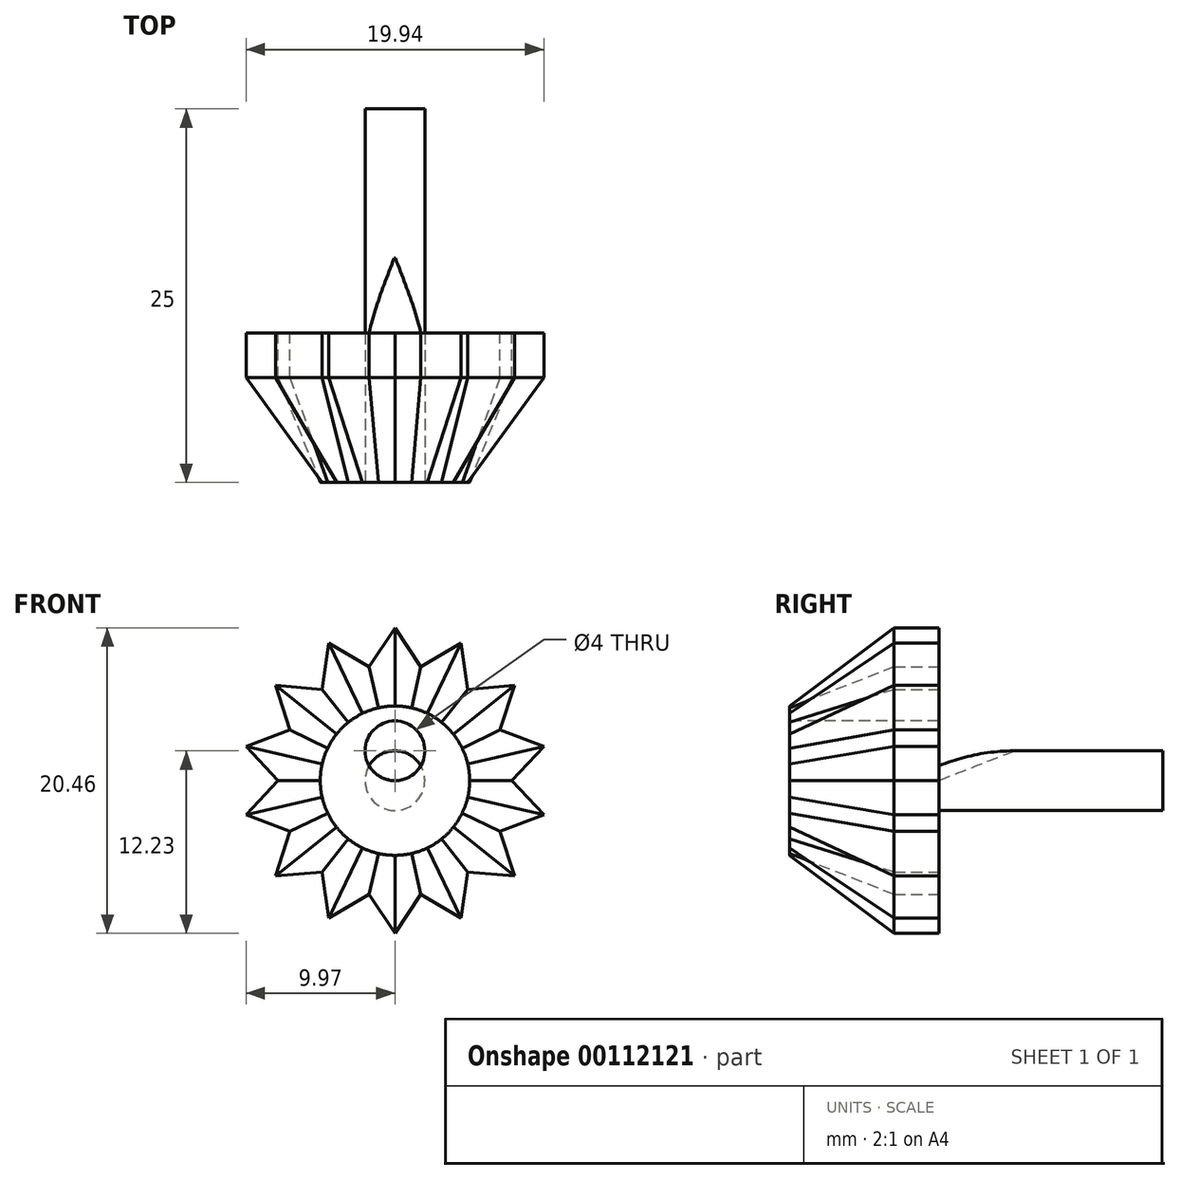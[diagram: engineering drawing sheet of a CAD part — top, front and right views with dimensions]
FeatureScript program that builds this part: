
annotation { "Feature Type Name" : "Feature", "Feature Type Description" : "" }
export const myFeature = defineFeature(function(context is Context, id is Id, definition is map)
    precondition{}
    {
        {
            var Q0;
            Q0=qCreatedBy(makeId("Front.planeOp"),FACE);
            var sketch = newSketch(context, id + "F0", { "sketchPlane" : qUnion([Q0])});
            skCircle(sketch, "E0", {"center": v(0, 0) * mm, "radius": 7.5 * mm, "construction": true});
            skLineSegment(sketch, "E1", {"start": v(-2, 7.23) * mm, "end": v(0, 10.23) * mm});
            skLineSegment(sketch, "E2", {"start": v(0, 10.23) * mm, "end": v(2, 7.23) * mm});
            skLineSegment(sketch, "E3", {"start": v(2, 7.23) * mm, "end": v(-2, 7.23) * mm, "construction": true});
            skLineSegment(sketch, "E4.1.0", {"start": v(-4.94, 5.64) * mm, "end": v(-4.44, 9.22) * mm});
            skLineSegment(sketch, "E4.1.1", {"start": v(-4.44, 9.22) * mm, "end": v(-1.33, 7.38) * mm});
            skLineSegment(sketch, "E4.2.0", {"start": v(-6.9, 2.94) * mm, "end": v(-8, 6.38) * mm});
            skLineSegment(sketch, "E4.2.1", {"start": v(-8, 6.38) * mm, "end": v(-4.4, 6.07) * mm});
            skLineSegment(sketch, "E4.3.0", {"start": v(-7.5, -0.34) * mm, "end": v(-9.97, 2.28) * mm});
            skLineSegment(sketch, "E4.3.1", {"start": v(-9.97, 2.28) * mm, "end": v(-6.6, 3.56) * mm});
            skLineSegment(sketch, "E4.4.0", {"start": v(-6.6, -3.56) * mm, "end": v(-9.97, -2.28) * mm});
            skLineSegment(sketch, "E4.4.1", {"start": v(-9.97, -2.28) * mm, "end": v(-7.5, 0.34) * mm});
            skLineSegment(sketch, "E4.5.0", {"start": v(-4.4, -6.07) * mm, "end": v(-8, -6.38) * mm});
            skLineSegment(sketch, "E4.5.1", {"start": v(-8, -6.38) * mm, "end": v(-6.9, -2.94) * mm});
            skLineSegment(sketch, "E4.6.0", {"start": v(-1.33, -7.38) * mm, "end": v(-4.44, -9.22) * mm});
            skLineSegment(sketch, "E4.6.1", {"start": v(-4.44, -9.22) * mm, "end": v(-4.94, -5.64) * mm});
            skLineSegment(sketch, "E4.7.0", {"start": v(2, -7.23) * mm, "end": v(0, -10.23) * mm});
            skLineSegment(sketch, "E4.7.1", {"start": v(0, -10.23) * mm, "end": v(-2, -7.23) * mm});
            skLineSegment(sketch, "E4.8.0", {"start": v(4.94, -5.64) * mm, "end": v(4.44, -9.22) * mm});
            skLineSegment(sketch, "E4.8.1", {"start": v(4.44, -9.22) * mm, "end": v(1.33, -7.38) * mm});
            skLineSegment(sketch, "E4.9.0", {"start": v(6.9, -2.94) * mm, "end": v(8, -6.38) * mm});
            skLineSegment(sketch, "E4.9.1", {"start": v(8, -6.38) * mm, "end": v(4.4, -6.07) * mm});
            skLineSegment(sketch, "E5.1.10.0", {"start": v(7.5, 0.34) * mm, "end": v(9.97, -2.28) * mm});
            skLineSegment(sketch, "E5.3.10.0", {"start": v(9.97, -2.28) * mm, "end": v(6.6, -3.56) * mm});
            skLineSegment(sketch, "E6.1.11.0", {"start": v(6.6, 3.56) * mm, "end": v(9.97, 2.28) * mm});
            skLineSegment(sketch, "E6.3.11.0", {"start": v(9.97, 2.28) * mm, "end": v(7.5, -0.34) * mm});
            skLineSegment(sketch, "E7.1.12.0", {"start": v(4.4, 6.07) * mm, "end": v(8, 6.38) * mm});
            skLineSegment(sketch, "E7.3.12.0", {"start": v(8, 6.38) * mm, "end": v(6.9, 2.94) * mm});
            skLineSegment(sketch, "E7.1.13.0", {"start": v(1.33, 7.38) * mm, "end": v(4.44, 9.22) * mm});
            skLineSegment(sketch, "E7.3.13.0", {"start": v(4.44, 9.22) * mm, "end": v(4.94, 5.64) * mm});
            skSolve(sketch);
        }
        {
            var Q0;
            Q0 = qSketchRegion(id + "F0", true);
            extrude(context, id + "F1", {"entities" : qUnion([Q0]), "depth" : 3 * mm});
        }
        {
            var Q0;
            Q0=makeQuery(id+"F1.opExtrude","CAP_FACE",FACE,{"disambiguationData":[OSD([sQuery(id+"F0.wireOp",EDGE,"fbJdyaIG-X2Uv-iruu-1M7H-KIjKJSGYAYfz"),sQuery(id+"F0.wireOp",EDGE,"E1"),sQuery(id+"F0.wireOp",EDGE,"E2"),sQuery(id+"F0.wireOp",EDGE,"E4.1.0"),sQuery(id+"F0.wireOp",EDGE,"E4.1.1"),sQuery(id+"F0.wireOp",EDGE,"E4.2.0"),sQuery(id+"F0.wireOp",EDGE,"E4.2.1"),sQuery(id+"F0.wireOp",EDGE,"E4.3.0"),sQuery(id+"F0.wireOp",EDGE,"E4.3.1"),sQuery(id+"F0.wireOp",EDGE,"E4.4.0"),sQuery(id+"F0.wireOp",EDGE,"E4.4.1"),sQuery(id+"F0.wireOp",EDGE,"E4.5.0"),sQuery(id+"F0.wireOp",EDGE,"E4.5.1"),sQuery(id+"F0.wireOp",EDGE,"E4.6.0"),sQuery(id+"F0.wireOp",EDGE,"E4.6.1"),sQuery(id+"F0.wireOp",EDGE,"E4.7.0"),sQuery(id+"F0.wireOp",EDGE,"E4.7.1"),sQuery(id+"F0.wireOp",EDGE,"E4.8.0"),sQuery(id+"F0.wireOp",EDGE,"E4.8.1"),sQuery(id+"F0.wireOp",EDGE,"E4.9.0"),sQuery(id+"F0.wireOp",EDGE,"E4.9.1"),sQuery(id+"F0.wireOp",EDGE,"E4.10.0"),sQuery(id+"F0.wireOp",EDGE,"E4.10.1"),sQuery(id+"F0.wireOp",EDGE,"E4.11.0"),sQuery(id+"F0.wireOp",EDGE,"E4.11.1"),sQuery(id+"F0.wireOp",EDGE,"E4.12.0"),sQuery(id+"F0.wireOp",EDGE,"E4.12.1"),sQuery(id+"F0.wireOp",EDGE,"E4.13.0"),sQuery(id+"F0.wireOp",EDGE,"E4.13.1"),sQuery(id+"F0.wireOp",EDGE,"E4.14.0"),sQuery(id+"F0.wireOp",EDGE,"E4.14.1"),sQuery(id+"F0.wireOp",EDGE,"E4.15.0"),sQuery(id+"F0.wireOp",EDGE,"E4.15.1")])],"isStart":true});
            var sketch = newSketch(context, id + "F2", { "sketchPlane" : qUnion([Q0])});
            skCircle(sketch, "E8", {"center": v(0, 0) * mm, "radius": 2 * mm});
            skSolve(sketch);
        }
        {
            var Q0;
            Q0 = qSketchRegion(id + "F2", true);
            extrude(context, id + "F3", {"entities" : qUnion([Q0]), "operationType" : NewBodyOperationType.ADD, "depth" : 15 * mm});
        }
        {
            var Q0;
            Q0=qCreatedBy(makeId("Front.planeOp"),FACE);
            cPlane(context, id + "F4", {"entities" : qUnion([Q0]), "cplaneType" : CPlaneType.OFFSET, "offset" : 10 * mm, "width" : 150 * mm, "height" : 150 * mm});
        }
        {
            var Q0;
            Q0=qCreatedBy(id+"F4.planeOp",FACE);
            var sketch = newSketch(context, id + "F5", { "sketchPlane" : qUnion([Q0])});
            skCircle(sketch, "E9", {"center": v(0, 0) * mm, "radius": 5 * mm});
            skSolve(sketch);
        }
        {
            var Q0;
            Q0=makeQuery(id+"F1.opExtrude","CAP_FACE",FACE,{"disambiguationData":[OSD([sQuery(id+"F0.wireOp",EDGE,"E1"),sQuery(id+"F0.wireOp",EDGE,"E2"),sQuery(id+"F0.wireOp",EDGE,"E4.1.0"),sQuery(id+"F0.wireOp",EDGE,"E4.1.1"),sQuery(id+"F0.wireOp",EDGE,"E4.2.0"),sQuery(id+"F0.wireOp",EDGE,"E4.2.1"),sQuery(id+"F0.wireOp",EDGE,"E4.3.0"),sQuery(id+"F0.wireOp",EDGE,"E4.3.1"),sQuery(id+"F0.wireOp",EDGE,"E4.4.0"),sQuery(id+"F0.wireOp",EDGE,"E4.4.1"),sQuery(id+"F0.wireOp",EDGE,"E4.5.0"),sQuery(id+"F0.wireOp",EDGE,"E4.5.1"),sQuery(id+"F0.wireOp",EDGE,"E4.6.0"),sQuery(id+"F0.wireOp",EDGE,"E4.6.1"),sQuery(id+"F0.wireOp",EDGE,"E4.7.0"),sQuery(id+"F0.wireOp",EDGE,"E4.7.1"),sQuery(id+"F0.wireOp",EDGE,"E4.8.0"),sQuery(id+"F0.wireOp",EDGE,"E4.8.1"),sQuery(id+"F0.wireOp",EDGE,"E4.9.0"),sQuery(id+"F0.wireOp",EDGE,"E4.9.1"),sQuery(id+"F0.wireOp",EDGE,"E5.1.10.0"),sQuery(id+"F0.wireOp",EDGE,"E5.3.10.0"),sQuery(id+"F0.wireOp",EDGE,"E6.1.11.0"),sQuery(id+"F0.wireOp",EDGE,"E6.3.11.0"),sQuery(id+"F0.wireOp",EDGE,"E7.1.12.0"),sQuery(id+"F0.wireOp",EDGE,"E7.3.12.0"),sQuery(id+"F0.wireOp",EDGE,"E7.1.13.0"),sQuery(id+"F0.wireOp",EDGE,"E7.3.13.0")])],"isStart":false});
            var sketch = newSketch(context, id + "F6", { "sketchPlane" : qUnion([Q0])});
            skLineSegment(sketch, "E10.0.0", {"start": v(8, -6.38) * mm, "end": v(7.04, -3.4) * mm});
            skLineSegment(sketch, "E10.0.1", {"start": v(7.04, -3.4) * mm, "end": v(9.97, -2.28) * mm});
            skLineSegment(sketch, "E10.0.2", {"start": v(9.97, -2.28) * mm, "end": v(7.82, 0) * mm});
            skLineSegment(sketch, "E10.0.3", {"start": v(7.82, 0) * mm, "end": v(9.97, 2.28) * mm});
            skLineSegment(sketch, "E10.0.4", {"start": v(9.97, 2.28) * mm, "end": v(7.04, 3.4) * mm});
            skLineSegment(sketch, "E10.0.5", {"start": v(7.04, 3.4) * mm, "end": v(8, 6.38) * mm});
            skLineSegment(sketch, "E10.0.6", {"start": v(8, 6.38) * mm, "end": v(4.87, 6.11) * mm});
            skLineSegment(sketch, "E10.0.7", {"start": v(4.87, 6.11) * mm, "end": v(4.44, 9.22) * mm});
            skLineSegment(sketch, "E10.0.8", {"start": v(4.44, 9.22) * mm, "end": v(1.74, 7.62) * mm});
            skLineSegment(sketch, "E10.0.9", {"start": v(1.74, 7.62) * mm, "end": v(0, 10.23) * mm});
            skLineSegment(sketch, "E10.0.10", {"start": v(0, 10.23) * mm, "end": v(-1.74, 7.62) * mm});
            skLineSegment(sketch, "E10.0.11", {"start": v(-1.74, 7.62) * mm, "end": v(-4.44, 9.22) * mm});
            skLineSegment(sketch, "E10.0.12", {"start": v(-4.44, 9.22) * mm, "end": v(-4.87, 6.11) * mm});
            skLineSegment(sketch, "E10.0.13", {"start": v(-4.87, 6.11) * mm, "end": v(-8, 6.38) * mm});
            skLineSegment(sketch, "E10.0.14", {"start": v(-8, 6.38) * mm, "end": v(-7.04, 3.4) * mm});
            skLineSegment(sketch, "E10.0.15", {"start": v(-7.04, 3.4) * mm, "end": v(-9.97, 2.28) * mm});
            skLineSegment(sketch, "E10.0.16", {"start": v(-9.97, 2.28) * mm, "end": v(-7.82, 0) * mm});
            skLineSegment(sketch, "E10.0.17", {"start": v(-7.82, 0) * mm, "end": v(-9.97, -2.28) * mm});
            skLineSegment(sketch, "E10.0.18", {"start": v(-9.97, -2.28) * mm, "end": v(-7.04, -3.4) * mm});
            skLineSegment(sketch, "E10.0.19", {"start": v(-7.04, -3.4) * mm, "end": v(-8, -6.38) * mm});
            skLineSegment(sketch, "E10.0.20", {"start": v(-8, -6.38) * mm, "end": v(-4.87, -6.11) * mm});
            skLineSegment(sketch, "E10.0.21", {"start": v(-4.87, -6.11) * mm, "end": v(-4.44, -9.22) * mm});
            skLineSegment(sketch, "E10.0.22", {"start": v(-4.44, -9.22) * mm, "end": v(-1.74, -7.62) * mm});
            skLineSegment(sketch, "E10.0.23", {"start": v(-1.74, -7.62) * mm, "end": v(0, -10.23) * mm});
            skLineSegment(sketch, "E10.0.24", {"start": v(0, -10.23) * mm, "end": v(1.74, -7.62) * mm});
            skLineSegment(sketch, "E10.0.25", {"start": v(1.74, -7.62) * mm, "end": v(4.44, -9.22) * mm});
            skLineSegment(sketch, "E10.0.26", {"start": v(4.44, -9.22) * mm, "end": v(4.87, -6.11) * mm});
            skLineSegment(sketch, "E10.0.27", {"start": v(4.87, -6.11) * mm, "end": v(8, -6.38) * mm});
            skSolve(sketch);
        }
        {
            var Q1;
            Q1 = qSketchRegion(id + "F6", true);
            var Q2;
            Q2 = qSketchRegion(id + "F5", true);
            loft(context, id + "F7", {"operationType" : NewBodyOperationType.ADD, "sheetProfilesArray" : [{ "sheetProfileEntities" : qUnion([Q1]) }, { "sheetProfileEntities" : qUnion([Q2]) }]});
        }
        {
            var Q0;
            Q0=makeQuery(id+"F7.opLoft","CAP_FACE",FACE,{"disambiguationData":[OSD([makeQuery(id+"F5.imprint","IMPRINT",FACE,{"disambiguationData":[TD([[makeQuery(id+"F5.imprint","IMPRINT",EDGE,{"derivedFrom":sQuery(id+"F5.wireOp",EDGE,"E9")}),1.0]])]})])],"isStart":true});
            var sketch = newSketch(context, id + "F8", { "sketchPlane" : qUnion([Q0])});
            skCircle(sketch, "E11", {"center": v(0, 2) * mm, "radius": 2 * mm});
            skSolve(sketch);
        }
        {
            var Q0;
            Q0 = qSketchRegion(id + "F8", true);
            extrude(context, id + "F9", {"entities" : qUnion([Q0]), "operationType" : NewBodyOperationType.REMOVE, "oppositeDirection" : true, "depth" : 10 * mm});
        }
        {
            var Q0;
            Q0=makeQuery(id+"F1.opExtrude","CAP_FACE",FACE,{"disambiguationData":[OSD([sQuery(id+"F0.wireOp",EDGE,"E1"),sQuery(id+"F0.wireOp",EDGE,"E2"),sQuery(id+"F0.wireOp",EDGE,"E4.1.0"),sQuery(id+"F0.wireOp",EDGE,"E4.1.1"),sQuery(id+"F0.wireOp",EDGE,"E4.2.0"),sQuery(id+"F0.wireOp",EDGE,"E4.2.1"),sQuery(id+"F0.wireOp",EDGE,"E4.3.0"),sQuery(id+"F0.wireOp",EDGE,"E4.3.1"),sQuery(id+"F0.wireOp",EDGE,"E4.4.0"),sQuery(id+"F0.wireOp",EDGE,"E4.4.1"),sQuery(id+"F0.wireOp",EDGE,"E4.5.0"),sQuery(id+"F0.wireOp",EDGE,"E4.5.1"),sQuery(id+"F0.wireOp",EDGE,"E4.6.0"),sQuery(id+"F0.wireOp",EDGE,"E4.6.1"),sQuery(id+"F0.wireOp",EDGE,"E4.7.0"),sQuery(id+"F0.wireOp",EDGE,"E4.7.1"),sQuery(id+"F0.wireOp",EDGE,"E4.8.0"),sQuery(id+"F0.wireOp",EDGE,"E4.8.1"),sQuery(id+"F0.wireOp",EDGE,"E4.9.0"),sQuery(id+"F0.wireOp",EDGE,"E4.9.1"),sQuery(id+"F0.wireOp",EDGE,"E5.1.10.0"),sQuery(id+"F0.wireOp",EDGE,"E5.3.10.0"),sQuery(id+"F0.wireOp",EDGE,"E6.1.11.0"),sQuery(id+"F0.wireOp",EDGE,"E6.3.11.0"),sQuery(id+"F0.wireOp",EDGE,"E7.1.12.0"),sQuery(id+"F0.wireOp",EDGE,"E7.3.12.0"),sQuery(id+"F0.wireOp",EDGE,"E7.1.13.0"),sQuery(id+"F0.wireOp",EDGE,"E7.3.13.0")])],"isStart":true});
            var sketch = newSketch(context, id + "F10", { "sketchPlane" : qUnion([Q0])});
            skArc(sketch, "E12.0", {"start": v(-1.73, 1) * mm, "mid": v(0, 4) * mm, "end": v(1.73, 1) * mm});
            skArc(sketch, "E13", {"start": v(-1.73, 1) * mm, "mid": v(0, 0) * mm, "end": v(1.73, 1) * mm});
            skSolve(sketch);
        }
        {
            var Q0;
            Q0=qCreatedBy(makeId("Front.planeOp"),FACE);
            cPlane(context, id + "F11", {"entities" : qUnion([Q0]), "cplaneType" : CPlaneType.OFFSET, "offset" : 5 * mm, "oppositeDirection" : true, "width" : 150 * mm, "height" : 150 * mm});
        }
        {
            var Q0;
            Q0=qCreatedBy(id+"F11.planeOp",FACE);
            var sketch = newSketch(context, id + "F12", { "sketchPlane" : qUnion([Q0])});
            skPoint(sketch, "E14.0", {"position": v(0, 2) * mm});
            skCircle(sketch, "E15", {"center": v(0, 2) * mm, "radius": 0.05 * mm});
            skSolve(sketch);
        }
        {
            var Q1;
            Q1 = qSketchRegion(id + "F10", true);
            var Q2;
            Q2 = qSketchRegion(id + "F12", true);
            loft(context, id + "F13", {"operationType" : NewBodyOperationType.REMOVE, "sheetProfilesArray" : [{ "sheetProfileEntities" : qUnion([Q1]) }, { "sheetProfileEntities" : qUnion([Q2]) }]});
        }
    });
